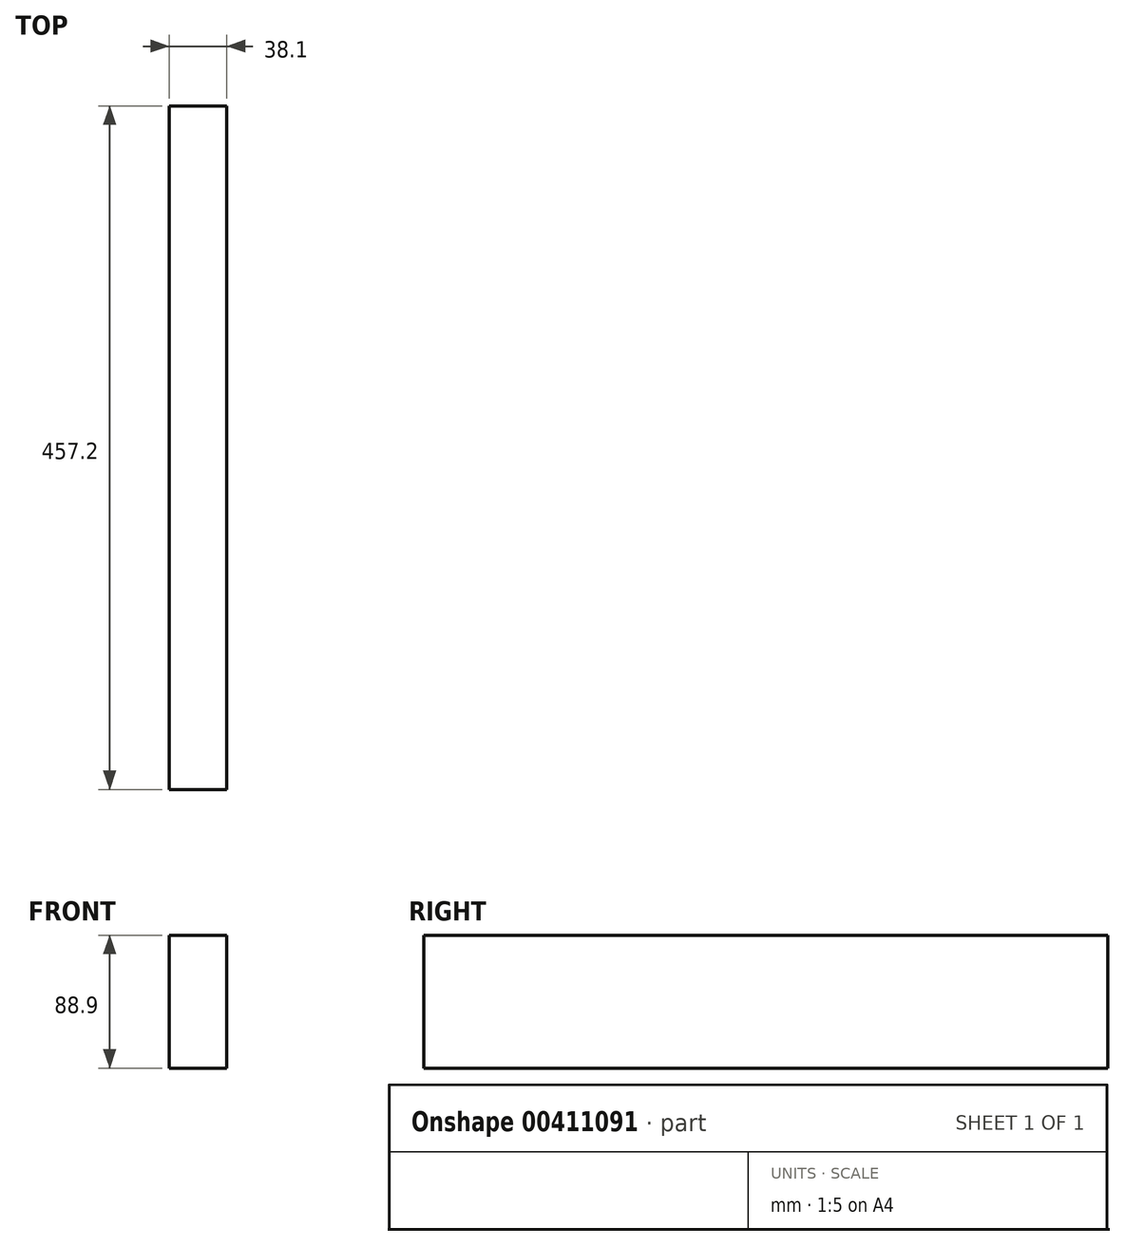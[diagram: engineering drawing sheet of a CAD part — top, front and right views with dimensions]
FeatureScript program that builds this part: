
annotation { "Feature Type Name" : "Feature", "Feature Type Description" : "" }
export const myFeature = defineFeature(function(context is Context, id is Id, definition is map)
    precondition{}
    {
        {
            var Q0;
            Q0=qCreatedBy(makeId("Front.planeOp"),FACE);
            var sketch = newSketch(context, id + "F0", { "sketchPlane" : qUnion([Q0])});
            skLineSegment(sketch, "E0.bottom", {"start": v(19.05, -44.45) * mm, "end": v(-19.05, -44.45) * mm});
            skLineSegment(sketch, "E0.top", {"start": v(19.05, 44.45) * mm, "end": v(-19.05, 44.45) * mm});
            skLineSegment(sketch, "E0.left", {"start": v(19.05, -44.45) * mm, "end": v(19.05, 44.45) * mm});
            skLineSegment(sketch, "E0.right", {"start": v(-19.05, -44.45) * mm, "end": v(-19.05, 44.45) * mm});
            skPoint(sketch, "E0.middle", {"position": v(0, 0) * mm});
            skSolve(sketch);
        }
        {
            var Q0;
            Q0=makeQuery(id+"F0.imprint","IMPRINT",FACE,{"disambiguationData":[TD([[makeQuery(id+"F0.imprint","IMPRINT",EDGE,{"derivedFrom":sQuery(id+"F0.wireOp",EDGE,"E0.bottom")}),-1.0]])]});
            extrude(context, id + "F1", {"entities" : qUnion([Q0]), "depth" : 457.2 * mm});
        }
    });
